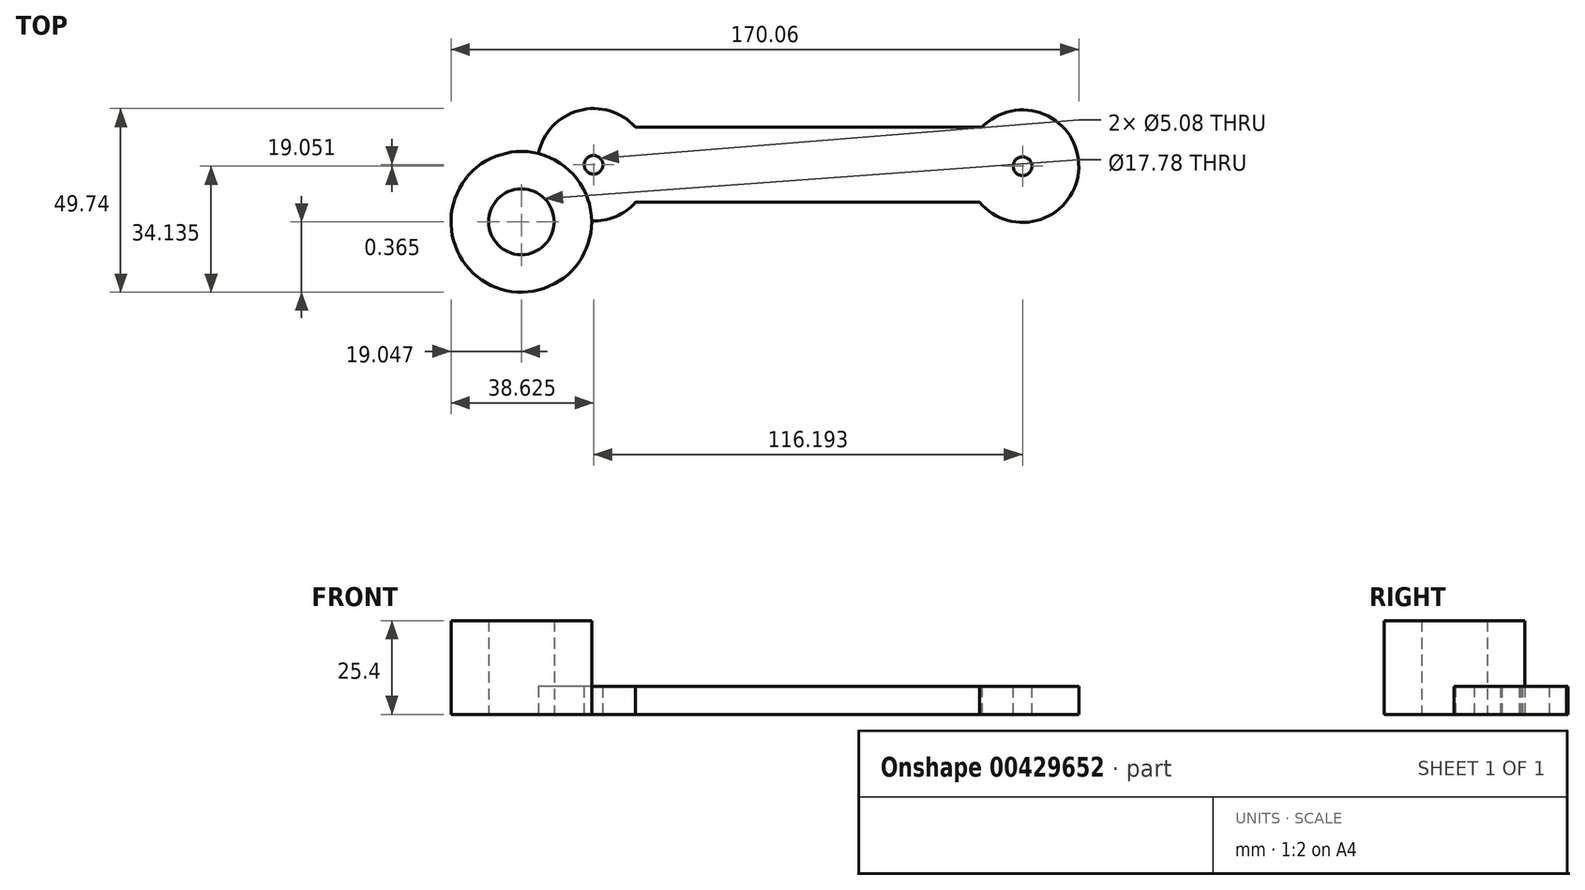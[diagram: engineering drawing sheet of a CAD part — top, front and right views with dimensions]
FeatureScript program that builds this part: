
annotation { "Feature Type Name" : "Feature", "Feature Type Description" : "" }
export const myFeature = defineFeature(function(context is Context, id is Id, definition is map)
    precondition{}
    {
        {
            var Q0;
            Q0=qCreatedBy(makeId("Top.planeOp"),FACE);
            var sketch = newSketch(context, id + "F0", { "sketchPlane" : qUnion([Q0])});
            skCircle(sketch, "E0", {"center": v(-268.24, 53.74) * mm, "radius": 15.24 * mm});
            skLineSegment(sketch, "E1.bottom", {"start": v(-279.26, 64.27) * mm, "end": v(-373.24, 64.27) * mm});
            skLineSegment(sketch, "E1.top", {"start": v(-279.26, 43.95) * mm, "end": v(-373.24, 43.95) * mm});
            skLineSegment(sketch, "E1.left", {"start": v(-279.26, 64.27) * mm, "end": v(-279.26, 43.95) * mm});
            skLineSegment(sketch, "E1.right", {"start": v(-373.24, 64.27) * mm, "end": v(-373.24, 43.95) * mm});
            skCircle(sketch, "E2", {"center": v(-384.44, 54.1) * mm, "radius": 15.24 * mm});
            skPoint(sketch, "E3", {"position": v(-373.24, 54.1) * mm});
            skSolve(sketch);
        }
        {
            var Q0;
            Q0 = qSketchRegion(id + "F0", true);
            extrude(context, id + "F1", {"entities" : qUnion([Q0]), "depth" : 7.62 * mm});
        }
        {
            var Q0;
            Q0=makeQuery(id+"F1.opExtrude","CAP_FACE",FACE,{"disambiguationData":[OSD([sQuery(id+"F0.wireOp",EDGE,"E0"),sQuery(id+"F0.wireOp",EDGE,"E1.bottom"),sQuery(id+"F0.wireOp",EDGE,"E1.top"),sQuery(id+"F0.wireOp",EDGE,"E2")])],"isStart":false});
            var sketch = newSketch(context, id + "F2", { "sketchPlane" : qUnion([Q0])});
            skCircle(sketch, "E4", {"center": v(-384.44, 54.1) * mm, "radius": 2.54 * mm});
            skCircle(sketch, "E5", {"center": v(-268.24, 53.74) * mm, "radius": 2.54 * mm});
            skSolve(sketch);
        }
        {
            var Q0;
            Q0 = qSketchRegion(id + "F2", true);
            extrude(context, id + "F3", {"entities" : qUnion([Q0]), "operationType" : NewBodyOperationType.REMOVE, "oppositeDirection" : true, "depth" : 25.4 * mm});
        }
        {
            var Q0;
            Q0=qCreatedBy(makeId("Top.planeOp"),FACE);
            var sketch = newSketch(context, id + "F4", { "sketchPlane" : qUnion([Q0])});
            skCircle(sketch, "E6", {"center": v(-404.01, 38.66) * mm, "radius": 19.05 * mm});
            skCircle(sketch, "E7", {"center": v(-404.01, 38.66) * mm, "radius": 8.9 * mm});
            skSolve(sketch);
        }
        {
            var Q0;
            Q0 = qSketchRegion(id + "F4", true);
            extrude(context, id + "F5", {"entities" : qUnion([Q0]), "operationType" : NewBodyOperationType.ADD, "depth" : 25.4 * mm});
        }
    });
